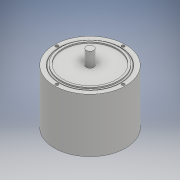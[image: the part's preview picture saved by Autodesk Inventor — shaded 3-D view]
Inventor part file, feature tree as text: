
AUTODESK INVENTOR PART (.ipt)
format: ipt  version: 2019.2 (Build 232265000, 265)  size: 166,400 bytes
history: native  units: mm
features: sketch x6, extrude x5, hole x1, pattern_circular x1, projected_geometry x1
ambient origin geometry x8: Origin, YZ Plane, XZ Plane, XY Plane, X Axis, Y Axis, Z Axis, Center Point
bodies: Solid1 (feature_tree)
feature tree (14):
  extrude  "Extrusion1"  Depth=120.0mm TaperAngle=0.0deg
  extrude  "Extrusion2"  Depth=109.5mm
  extrude  "Extrusion3"  Depth=2.5mm
  hole  "Hole1"  [1 undecoded]
  pattern_circular  "Circular Pattern1"  Count=4 Angle=360.0deg
  extrude  "Extrusion4"  Depth=120.0mm
  extrude  "Extrusion5"  Depth=10.0mm TaperAngle=0.0deg
  sketch  "Sketch1"  dims[d0=145.0mm d1=120.0mm d2=0.0mm]
  sketch  "Sketch2"  dims[d3=118.0mm d4=109.5mm]
  sketch  "Sketch3"  dims[d5=2.5mm d6=0.0mm d7=15.0mm]
  sketch  "Sketch4"  dims[d8=30.0mm d9=0.0mm d10=67.5mm]
  sketch  "Sketch5"  dims[d11=6.0mm d12=6.0mm d13=4.0mm d14=2.0mm d15=90.0deg d16=8.0mm d17=20.594885mm d18=40.0mm d19=360.0deg]
  sketch  "Sketch6"  dims[d21=124.0mm d22=1.0mm d23=10.0mm d24=0.0mm d25=7.3mm d26=0.0mm d27=120.0mm]
  projected_geometry  "Projected Loop1"
note: 1 required parameter value undecoded (feature->parameter linkage not recoverable at this tier; creation-order binding heuristic only, values carry confidence <= 0.55)
